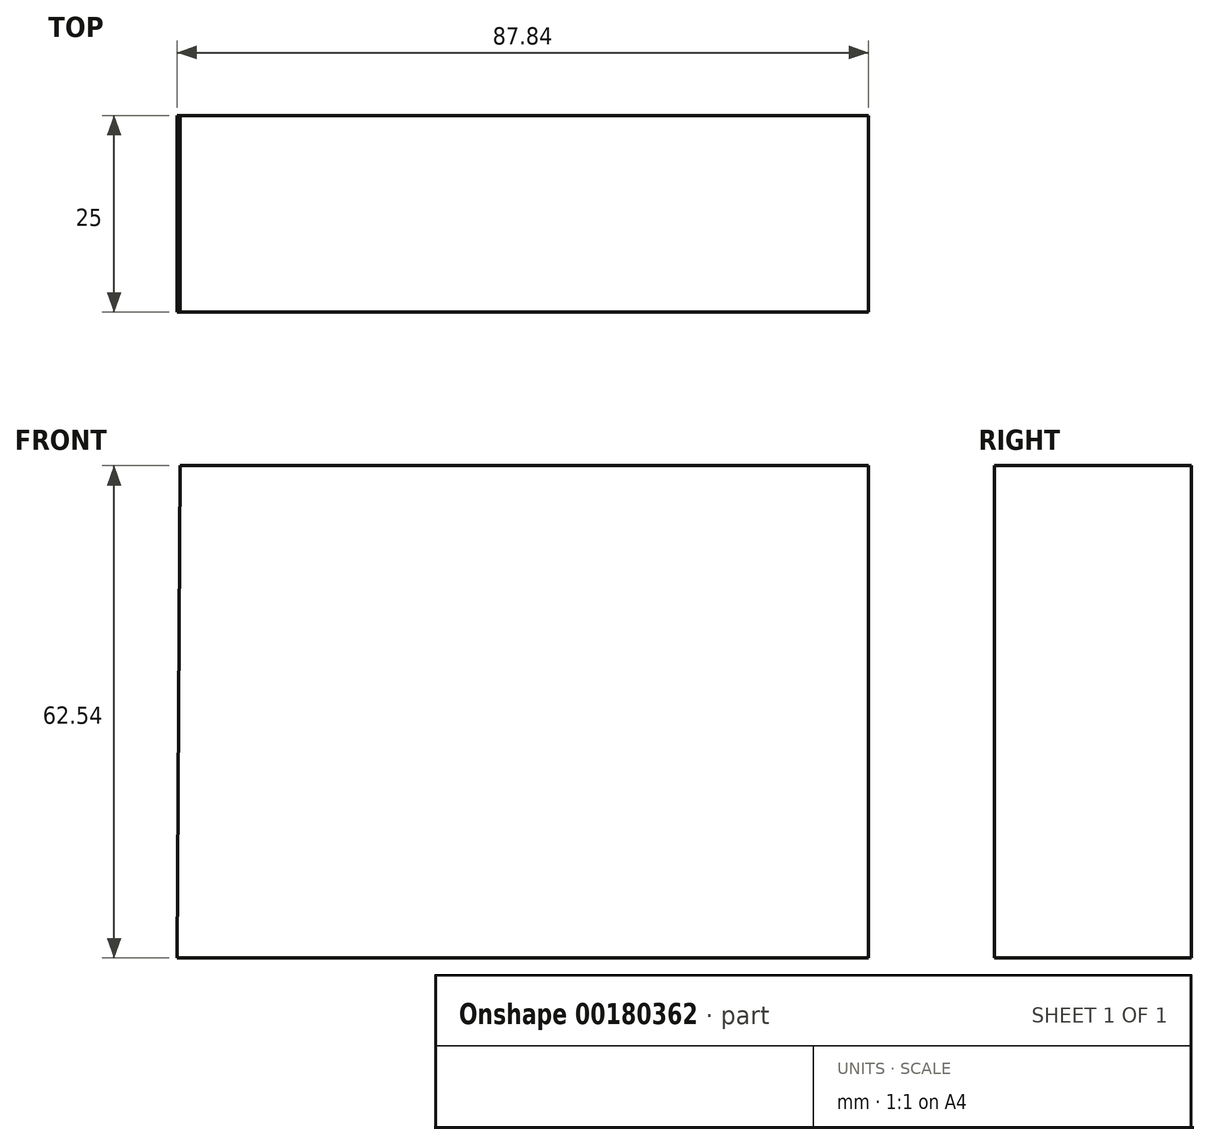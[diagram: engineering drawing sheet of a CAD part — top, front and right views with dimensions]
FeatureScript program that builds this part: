
annotation { "Feature Type Name" : "Feature", "Feature Type Description" : "" }
export const myFeature = defineFeature(function(context is Context, id is Id, definition is map)
    precondition{}
    {
        {
            var Q0;
            Q0=qCreatedBy(makeId("Front.planeOp"),FACE);
            var sketch = newSketch(context, id + "F0", { "sketchPlane" : qUnion([Q0])});
            skLineSegment(sketch, "E0", {"start": v(-47.11, 42.8) * mm, "end": v(40.32, 42.8) * mm});
            skLineSegment(sketch, "E1", {"start": v(40.32, 42.8) * mm, "end": v(40.32, -19.75) * mm});
            skLineSegment(sketch, "E2", {"start": v(40.32, -19.75) * mm, "end": v(-47.52, -19.75) * mm});
            skLineSegment(sketch, "E3", {"start": v(-47.52, -19.75) * mm, "end": v(-47.11, 42.8) * mm});
            skSolve(sketch);
        }
        {
            var Q0;
            Q0=makeQuery(id+"F0.imprint","IMPRINT",FACE,{"disambiguationData":[TD([[makeQuery(id+"F0.imprint","IMPRINT",EDGE,{"derivedFrom":sQuery(id+"F0.wireOp",EDGE,"E0")}),-1.0]])]});
            var Q1;
            Q1 = qSketchRegion(id + "F0", true);
            extrude(context, id + "F1", {"entities" : qUnion([Q0, Q1]), "depth" : 25 * mm});
        }
    });
